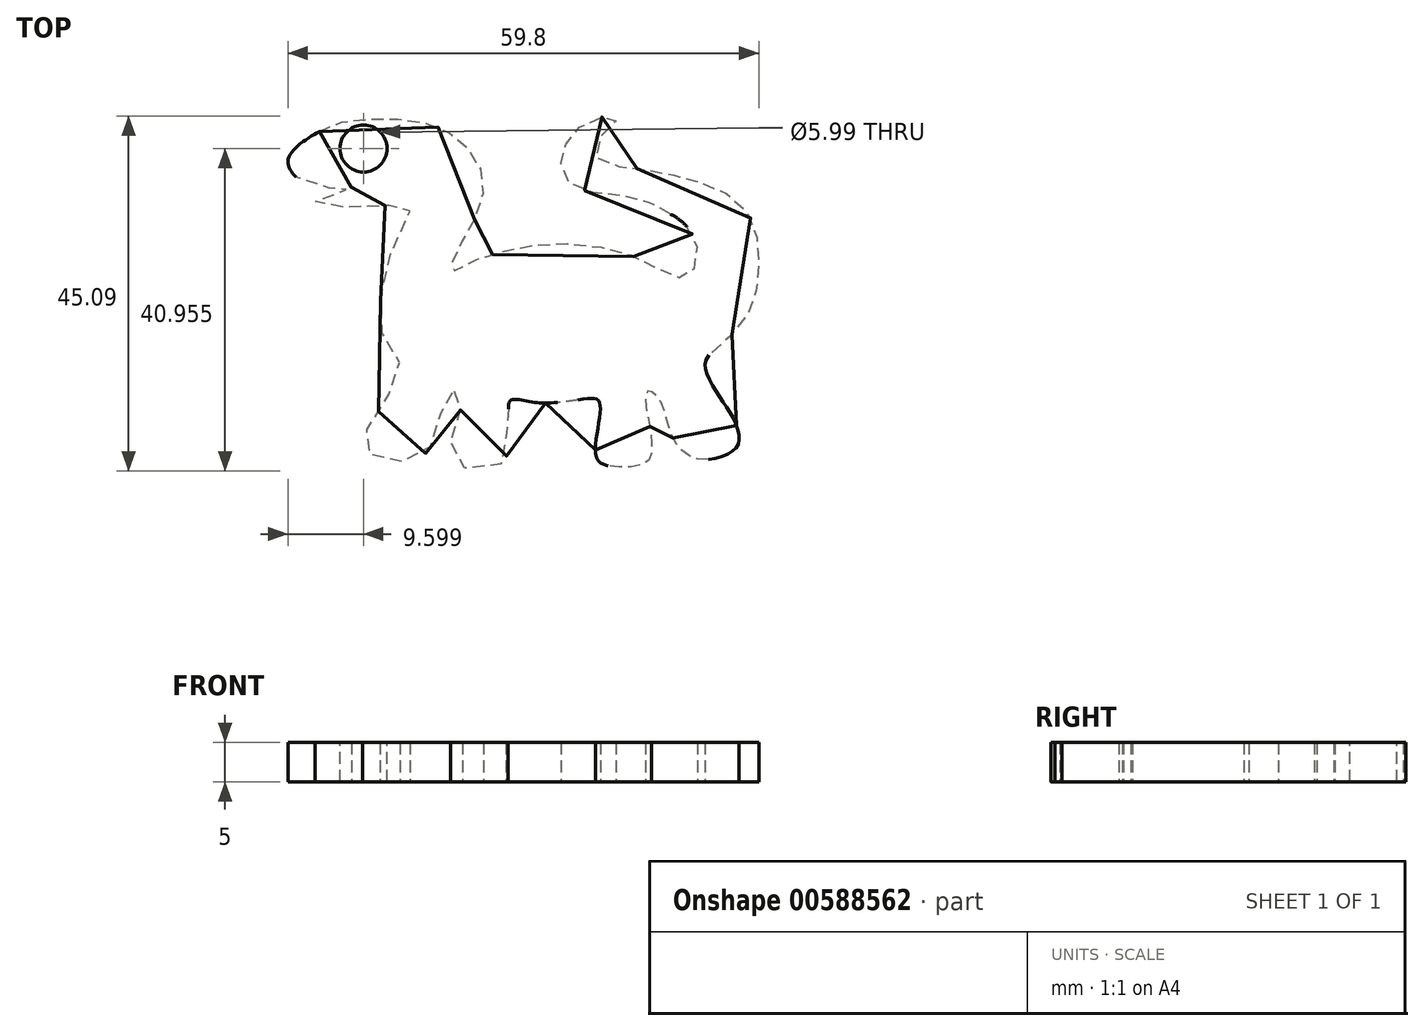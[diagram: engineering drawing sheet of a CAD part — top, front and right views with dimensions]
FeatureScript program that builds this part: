
annotation { "Feature Type Name" : "Feature", "Feature Type Description" : "" }
export const myFeature = defineFeature(function(context is Context, id is Id, definition is map)
    precondition{}
    {
        {
            var Q0;
            Q0=qCreatedBy(makeId("Top.planeOp"),FACE);
            var sketch = newSketch(context, id + "F0", { "sketchPlane" : qUnion([Q0])});
            skFitSpline(sketch, "E0", {"points": [v(-56.47, 50.6) * mm, v(-53.25, 51.88) * mm, v(-48.42, 52.22) * mm, v(-43.93, 51.88) * mm, v(-40.11, 50.53) * mm, v(-37.57, 48.4) * mm, v(-35.8, 45.1) * mm, v(-35.96, 41.54) * mm, v(-37.66, 37.81) * mm, v(-39.52, 34.42) * mm, v(-39.77, 32.64) * mm, v(-38.76, 33.32) * mm, v(-34.6, 34.93) * mm, v(-29.6, 36.12) * mm, v(-23, 36.2) * mm, v(-17.06, 34.93) * mm, v(-13.33, 33.07) * mm, v(-9.94, 32.05) * mm, v(-8.67, 33.66) * mm, v(-8.58, 36.46) * mm, v(-10.28, 39) * mm, v(-12.74, 40.6) * mm, v(-16.21, 42.13) * mm, v(-21.98, 42.9) * mm, v(-25.28, 44.68) * mm, v(-25.7, 47.22) * mm, v(-24.86, 49.5) * mm, v(-22.4, 51.8) * mm, v(-19.1, 52.47) * mm, v(-18.84, 51.88) * mm, v(-21.13, 49.42) * mm, v(-21.13, 47.13) * mm, v(-16.8, 45.95) * mm, v(-12.14, 45.19) * mm, v(-8, 44.08) * mm, v(-3.33, 41.71) * mm, v(-1.04, 37.81) * mm, v(-0.7, 32.81) * mm, v(-1.3, 29.17) * mm, v(-3.5, 25.35) * mm, v(-7.14, 21.96) * mm, v(-7.31, 20.01) * mm, v(-5.62, 16.88) * mm, v(-3.84, 14) * mm, v(-3.16, 11.28) * mm, v(-4.18, 9.84) * mm, v(-7.82, 8.91) * mm, v(-10.28, 9.93) * mm, v(-11.72, 12.05) * mm, v(-13.08, 16.2) * mm, v(-14, 17.3) * mm, v(-14.77, 17.64) * mm, v(-15.03, 16.03) * mm, v(-14.52, 13.23) * mm, v(-14.26, 10.7) * mm, v(-14.77, 8.66) * mm, v(-18.42, 7.98) * mm, v(-21.04, 8.74) * mm, v(-21.3, 11.62) * mm, v(-20.79, 15.52) * mm, v(-21.13, 16.54) * mm, v(-22.65, 16.62) * mm, v(-26.98, 16.11) * mm, v(-30.28, 16.37) * mm, v(-32.23, 16.37) * mm, v(-32.49, 14.5) * mm, v(-32.74, 13.06) * mm, v(-32.57, 9.84) * mm, v(-34.69, 7.64) * mm, v(-39.01, 8.4) * mm, v(-39.77, 11.11) * mm, v(-38.76, 14.59) * mm, v(-38.42, 17.3) * mm, v(-39.44, 17.8) * mm, v(-40.45, 16.28) * mm, v(-41.72, 12.8) * mm, v(-43, 9.67) * mm, v(-46.22, 8.66) * mm, v(-49.7, 9.33) * mm, v(-50.96, 11.03) * mm, v(-49.52, 14.17) * mm, v(-46.72, 19) * mm, v(-46.38, 21.54) * mm, v(-48.42, 24.76) * mm, v(-48.67, 29.34) * mm, v(-47.83, 34.08) * mm, v(-44.94, 40.52) * mm, v(-45.54, 41.2) * mm, v(-48.59, 41.12) * mm, v(-54.78, 41.03) * mm, v(-56.98, 41.63) * mm, v(-55.88, 42.3) * mm, v(-52.4, 43.5) * mm, v(-55.7, 43.4) * mm, v(-59.18, 44.6) * mm, v(-60.4, 47.13) * mm, v(-56.47, 50.6) * mm]});
            skSolve(sketch);
        }
        {
            var Q0;
            Q0=makeQuery(id+"F0.imprint","IMPRINT",FACE,{"disambiguationData":[TD([[makeQuery(id+"F0.imprint","IMPRINT",EDGE,{"derivedFrom":sQuery(id+"F0.wireOp",EDGE,"E0")}),-1.0]])]});
            extrude(context, id + "F1", {"entities" : qUnion([Q0]), "depth" : 5 * mm, "offsetDistance" : 25 * mm});
        }
        {
            var Q0;
            Q0=makeQuery(id+"F1.opExtrude","CAP_FACE",FACE,{"disambiguationData":[OSD([sQuery(id+"F0.wireOp",EDGE,"E0")])],"isStart":false});
            var sketch = newSketch(context, id + "F2", { "sketchPlane" : qUnion([Q0])});
            skCircle(sketch, "E1", {"center": v(-50.86, 48.43) * mm, "radius": 3 * mm});
            skSolve(sketch);
        }
        {
            var Q0;
            Q0=makeQuery(id+"F2.imprint","IMPRINT",FACE,{"disambiguationData":[TD([[makeQuery(id+"F2.imprint","IMPRINT",EDGE,{"derivedFrom":sQuery(id+"F2.wireOp",EDGE,"E1")}),1.0]])]});
            extrude(context, id + "F3", {"entities" : qUnion([Q0]), "operationType" : NewBodyOperationType.REMOVE, "oppositeDirection" : true, "depth" : 5 * mm, "offsetDistance" : 25 * mm});
        }
    });
